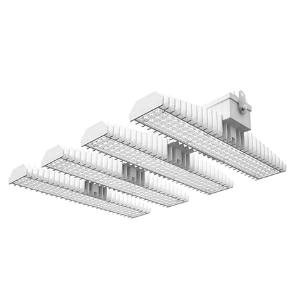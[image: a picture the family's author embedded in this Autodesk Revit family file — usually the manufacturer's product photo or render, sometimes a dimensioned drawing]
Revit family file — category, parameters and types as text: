
# Revit family: 3f_filippi_-_3f_lem_ht_medio_3f_filippi_-_59039_a0811_-_3f_lem_4_ht_led_120_cr_medio___vt_1423
name_source: partatom
category: Lighting Fixtures
units: mm (PartAtom-declared; Revit-internal decimal feet)

## family parameters
Cut with Voids When Loaded = No
Host = Face
Light Source = No
Part Type = Normal
Room Calculation Point = No
Round Connector Dimension = Use Diameter
Shared = No

## types (1)
- 3F Filippi - 3F LEM HT Medio (1 x LED, 19813 lm, 136 W, 4000 K)
    Apparent Load = 136 VA
    Approval mark = ENEC
    CIE Flux Codes = 83 96 99 100 100
    Color Rendering = 80
    Color Temperature = 4000 K
    Control Gear = Electronic ballast
    Default Elevation = 1800 mm
    Description = Industrial luminaire with high light output and high luminous efficiency designed with the most innovative technologies for environments with temperature up to 70°C.

ILLUMINOTECHNICAL
Luminous efficiency 100% (DLOR 99%, ULOR 1%).
Initial luminous flux of the luminaire 19813 lm.
Medium distribution with rectangular shape.
Installation Interdistance Transv.D = 1.02 x hu - Long.D = 1.06 x hu.
Tabular UGR (CIE 117 - 4H-8H; S=0.25H; 70/50/20): RUG 17.4 - 17.
Beam angle: 65° - 67°.
Luminous efficacy 146 lm/W.
Lifetime (L93/B10): 30000 h. (tq+25°C)
Lifetime (L90/B10): 50000 h. (tq+25°C)
Lifetime (L85/B10): 80000 h. (tq+25°C)
Lifetime (L80/B10): 100000 h. (tq+25°C)
Lifetime (L85/B10): 50000 h. (tq+70°C)
Sudden decreased luminous flux after 50000 hours: 0% (C0).
Photobiological safety in compliance with IEC/TR 62778: RG0 risk exempt, (IEC 62471).
In compliance with IEC/EN 62722-2-1 - IEC/EN 62717 standards.
Luminous flux at +70°C: -13.5%.

SOURCE
4 Mid-Power linear LED modules 30W/840.
Energy efficiency class (UE 2019/2020 - UE 2019/2015): C.
CIE 13.3 Colour rendering index: CRI >80 (R9 <50%).
IES TM-30 Fidelity Index: Rf = 84 Rg = 95.
CCT nominal colour temperature 4000 K.
Colour initial tolerance (MacAdam): SDCM 3.

MECHANICAL
Passive modular heatsinks in die-casted aluminium, painted in white colour.
To optimize the thermal management of the LED module, the heatsinks are oversized and provided with self-cleaning of cooling fins.
Wiring body in aluminium and galvanised steel anchored solidly to the sinks and thermally separated.
3F Lens lenses with high luminous efficiency, transparent polycarbonate, fixed to the LED modules.
Fixing brackets in stainless steel.
Luminaire with limited surface temperature. - D - (EN 60598-2-24)
Dimensions: 757x542 mm, height 133 mm. Weight 18.188 kg.
IP65 protection degree.
Mechanical strength to impacts IK08 (5 joule).
Glow-wire test resistance 850°C.

ELECTRICAL
Halogen Free electronic wiring 230V-50/60Hz, power factor 0.97, THD <25%, constant output current, class I, 2 driver.
Power of the luminaire 136 W.
CE - IEC 60598-1 - EN 60598-1.
SAFE FLICKER: PstLM=<1 and SVM=<0.4 (IEC TR 61547-1 and IEC TR 63158), to ensure a more comfortable and safe light.
Luminaire compliant with EN 60598-2-22 for power supply from a centralised emergency system CPSS (Central Power Supply System), not incorporated in the luminaire - high risk areas excluded. The default power and flux are 100% in AC and 100% in DC.
Ambient temperature from -30°C to +70°C.
Temperature class T6 max 85°C.
Quick connection via M20 3P connector with 9-13 mm tightening range.
Power unit positioned on a separate compartment by the LED module to ensure optimum temperatures of cabling components, to be inspectable and maintainable.
Relative humidity UR: <85%.

INSTALLATION
Ceiling / Suspended / Wall.
All accessories dedicated to this product are available on the Catalog and on our website www.3F-Filippi.com.

ACCESSORIES
A0811 - VT transparent glass, tempered, not flammable, with sealing gasket.
One required for each light module. The pack contains 10 pieces.

APPLICATIONS
In commercial environments, exhibition and industrial areas, stores, open areas.
Applications with high ambient temperature up to 70°C.

WARNING
Fixture not suitable for cold stores with an ambient temperature <0°C and/or relative humidity >85%.
Luminaire designed for disposal/recycling at end-of-life.
Replaceable (LED only) light source by a professional. Replaceable control gear by a professional.
    Height = 133 mm  [stored 0.436352 ft]
    Lamp = 1 x LED
    Lamp Light Flux = 19813 lm
    Lamp Power = 136 W
    Lamp count = 1
    Length = 757 mm
    Lifetime = 50000 h
    Luminous efficacy = 146 lm/W
    Manufacturer = 3F Filippi
    ModVariant = No
    Model = 3F Filippi - 59039+A0811 - 3F LEM 4 HT LED 120 CR MEDIO + VT
    Mounting Place = Ceiling
    Mounting Type = Pendant
    Number of Poles = 1
    OnlyDefault = Yes
    Power Factor = 1
    Product Name = 3F Filippi - 3F LEM HT Medio
    Product group = pendant luminaire
    ProductGroupID = 9
    Protection Class = Protection class I
    Protection Degree = IP 65
    RLX_Detail_Level = 1
    RLX_Emergency_Light_Flux = 0 lm
    RLX_Emergency_Type = 0
    RLX_Emergency_Type_DB = No
    RlxData = <blob elided: 117373 chars, md5=e3414a9b>
    Socket = socket
    Standby Power = 0 W
    System Light Flux = 19813 lm
    System Power = 136 W
    Type Comments = Product without accessories
    Type Image = 3f_filippi_-_lem_4__a0811.jpg
    URL = http://relux.com
    VarID = ---
    Voltage = 0 V
    Weight = 0.00 kg
    Width = 542 mm

note: [stored X ft] marks values corroborated as IEEE doubles in the binary element streams (Revit-internal decimal feet)

## geometry (parser evidence)
native form markers: Blend x4, Sweep x13
no freeform markers — native parametric forms only
